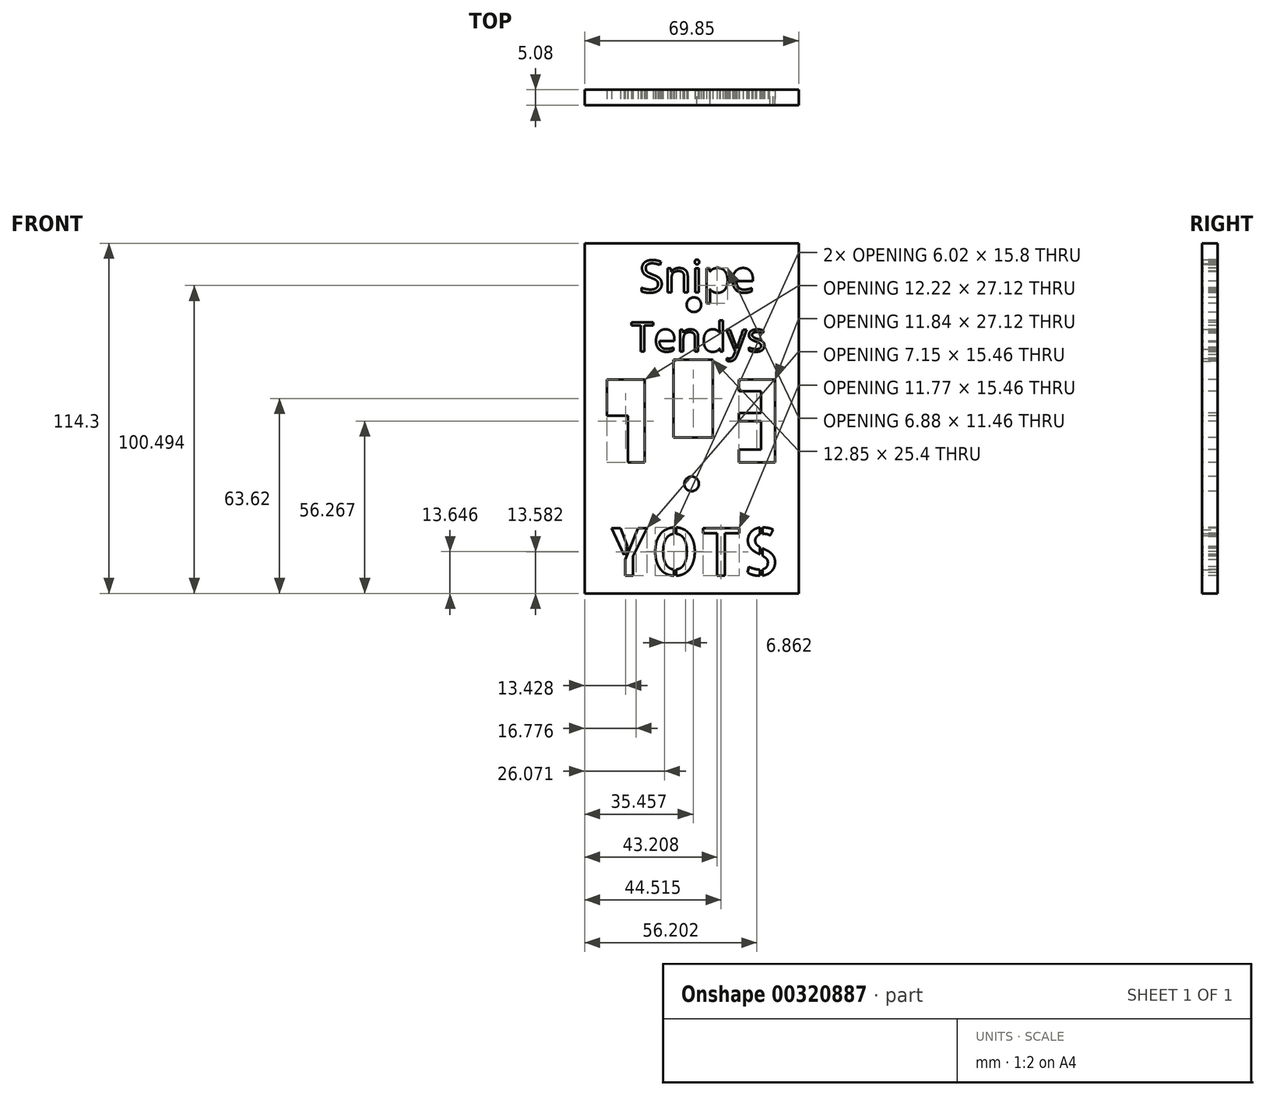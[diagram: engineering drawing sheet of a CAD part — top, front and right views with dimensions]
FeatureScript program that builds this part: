
annotation { "Feature Type Name" : "Feature", "Feature Type Description" : "" }
export const myFeature = defineFeature(function(context is Context, id is Id, definition is map)
    precondition{}
    {
        {
            var Q0;
            Q0=qCreatedBy(makeId("Front.planeOp"),FACE);
            var sketch = newSketch(context, id + "F0", { "sketchPlane" : qUnion([Q0])});
            skLineSegment(sketch, "E0", {"start": v(-41.88, 63.38) * mm, "end": v(-41.88, -50.92) * mm});
            skLineSegment(sketch, "E1", {"start": v(-41.88, -50.92) * mm, "end": v(27.97, -50.92) * mm});
            skLineSegment(sketch, "E2", {"start": v(27.97, -50.92) * mm, "end": v(27.97, 63.38) * mm});
            skLineSegment(sketch, "E3", {"start": v(27.97, 63.38) * mm, "end": v(-41.88, 63.38) * mm});
            skLineSegment(sketch, "E4", {"start": v(-12.85, 25.4) * mm, "end": v(-12.85, 0) * mm});
            skLineSegment(sketch, "E5", {"start": v(-12.85, 0) * mm, "end": v(0, 0) * mm});
            skLineSegment(sketch, "E6", {"start": v(0, 0) * mm, "end": v(0, 25.4) * mm});
            skLineSegment(sketch, "E7", {"start": v(0, 25.4) * mm, "end": v(-12.85, 25.4) * mm});
            skCircle(sketch, "E8", {"center": v(-6.2, 43.3) * mm, "radius": 2.38 * mm});
            skCircle(sketch, "E9", {"center": v(-6.95, -15.16) * mm, "radius": 2.38 * mm});
            skLineSegment(sketch, "E10", {"start": v(-34.56, 18.9) * mm, "end": v(-22.34, 18.9) * mm});
            skLineSegment(sketch, "E11", {"start": v(-22.34, 18.9) * mm, "end": v(-22.34, -8.21) * mm});
            skLineSegment(sketch, "E12", {"start": v(-22.34, -8.21) * mm, "end": v(-27.69, -8.21) * mm});
            skLineSegment(sketch, "E13", {"start": v(-27.69, -8.21) * mm, "end": v(-27.69, 7.07) * mm});
            skLineSegment(sketch, "E14", {"start": v(-27.69, 7.07) * mm, "end": v(-34.56, 7.07) * mm});
            skLineSegment(sketch, "E15", {"start": v(-34.56, 7.07) * mm, "end": v(-34.56, 18.9) * mm});
            skLineSegment(sketch, "E16", {"start": v(8.4, 18.9) * mm, "end": v(20.24, 18.9) * mm});
            skLineSegment(sketch, "E17", {"start": v(20.24, 18.9) * mm, "end": v(20.24, -8.21) * mm});
            skLineSegment(sketch, "E18", {"start": v(20.24, -8.21) * mm, "end": v(8.4, -8.21) * mm});
            skLineSegment(sketch, "E19", {"start": v(8.4, -8.21) * mm, "end": v(8.4, -4.01) * mm});
            skLineSegment(sketch, "E20", {"start": v(8.4, -4.01) * mm, "end": v(15.66, -4.01) * mm});
            skLineSegment(sketch, "E21", {"start": v(15.66, -4.01) * mm, "end": v(15.66, 5.35) * mm});
            skPoint(sketch, "E21.endSnap0", {"position": v(20.24, 5.35) * mm});
            skLineSegment(sketch, "E22", {"start": v(15.66, 5.35) * mm, "end": v(8.4, 5.35) * mm});
            skLineSegment(sketch, "E23", {"start": v(8.4, 5.35) * mm, "end": v(8.4, 8.02) * mm});
            skLineSegment(sketch, "E24", {"start": v(8.4, 8.02) * mm, "end": v(15.66, 8.02) * mm});
            skLineSegment(sketch, "E25", {"start": v(15.66, 8.02) * mm, "end": v(15.66, 15.09) * mm});
            skLineSegment(sketch, "E26", {"start": v(15.66, 15.09) * mm, "end": v(8.4, 15.09) * mm});
            skLineSegment(sketch, "E27", {"start": v(8.4, 15.09) * mm, "end": v(8.4, 18.9) * mm});
            skText(sketch, "E28", { "text": "YOTS\n", "fontName": "AllertaStencil-Regular.ttf"});
            skText(sketch, "E29", { "text": "Snipe", "fontName": "OpenSans-Regular.ttf"});
            skText(sketch, "E30", { "text": "Tendys", "fontName": "OpenSans-Regular.ttf"});
            const initialGuessF0  = {"E28": [-0.03418, -0.04507, 1, 0, 0.01547], "E29": [-0.02403, 0.04735, 1, 0, 0.01051], "E30": [-0.02667, 0.02806, 1, 0, 0.00955]};
            skSetInitialGuess(sketch, initialGuessF0);
            skSolve(sketch);
        }
        {
            var Q0;
            Q0 = qSketchRegion(id + "F0", true);
            extrude(context, id + "F1", {"entities" : qUnion([Q0]), "oppositeDirection" : true, "depth" : 5.08 * mm});
        }
    });
